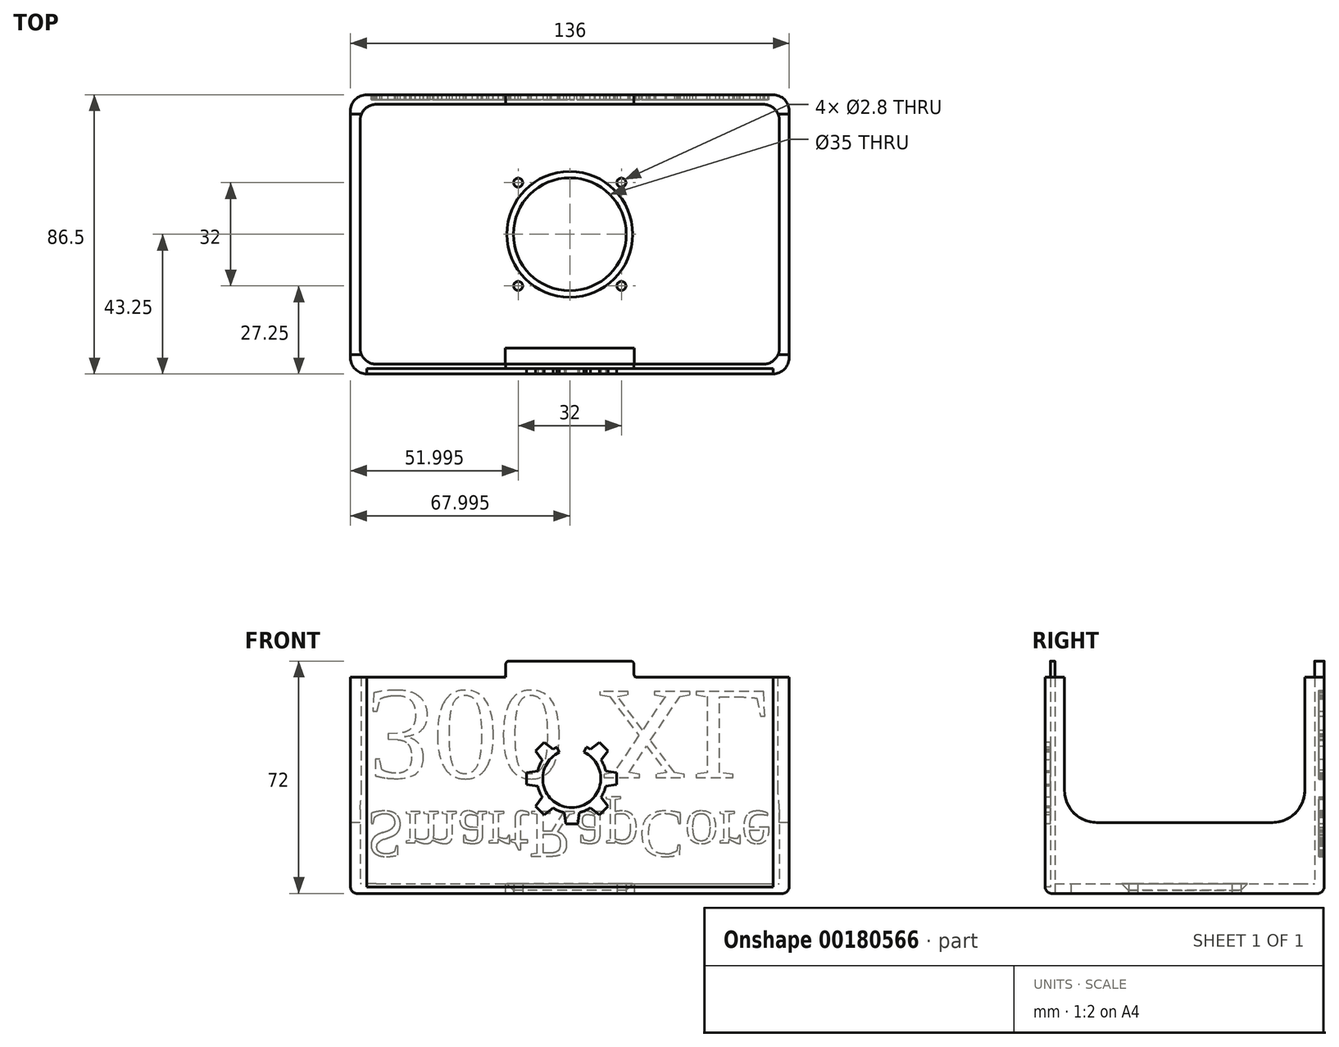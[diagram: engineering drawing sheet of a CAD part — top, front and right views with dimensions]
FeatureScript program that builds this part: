
annotation { "Feature Type Name" : "Feature", "Feature Type Description" : "" }
export const myFeature = defineFeature(function(context is Context, id is Id, definition is map)
    precondition{}
    {
        {
            var Q0;
            Q0=qCreatedBy(makeId("Top.planeOp"),FACE);
            var sketch = newSketch(context, id + "F0", { "sketchPlane" : qUnion([Q0])});
            skLineSegment(sketch, "E0.bottom", {"start": v(-60.37, 0) * mm, "end": v(69.63, 0) * mm});
            skLineSegment(sketch, "E0.top", {"start": v(-60.37, 92.5) * mm, "end": v(69.63, 92.5) * mm});
            skLineSegment(sketch, "E0.left", {"start": v(-60.37, 0) * mm, "end": v(-60.37, 92.5) * mm});
            skLineSegment(sketch, "E0.right", {"start": v(69.63, 0) * mm, "end": v(69.63, 92.5) * mm});
            skLineSegment(sketch, "E1.top", {"start": v(-60.37, 7) * mm, "end": v(69.63, 7) * mm});
            skLineSegment(sketch, "E1.left", {"start": v(-60.37, 0) * mm, "end": v(-60.37, 7) * mm});
            skLineSegment(sketch, "E1.right", {"start": v(69.63, 0) * mm, "end": v(69.63, 7) * mm});
            skLineSegment(sketch, "E2.bottom", {"start": v(-15.37, 7) * mm, "end": v(24.63, 7) * mm});
            skLineSegment(sketch, "E2.top", {"start": v(-15.37, 12) * mm, "end": v(24.63, 12) * mm});
            skLineSegment(sketch, "E2.left", {"start": v(-15.37, 7) * mm, "end": v(-15.37, 12) * mm});
            skLineSegment(sketch, "E2.right", {"start": v(24.63, 7) * mm, "end": v(24.63, 12) * mm});
            skPoint(sketch, "E3", {"position": v(4.63, 92.5) * mm});
            skPoint(sketch, "E4", {"position": v(4.63, 12) * mm});
            skLineSegment(sketch, "E5.top", {"start": v(-60.37, 87.5) * mm, "end": v(69.63, 87.5) * mm});
            skLineSegment(sketch, "E5.left", {"start": v(-60.37, 92.5) * mm, "end": v(-60.37, 87.5) * mm});
            skLineSegment(sketch, "E5.right", {"start": v(69.63, 92.5) * mm, "end": v(69.63, 87.5) * mm});
            skCircle(sketch, "E6", {"center": v(4.63, 47.25) * mm, "radius": 17.5 * mm});
            skCircle(sketch, "E7", {"center": v(20.63, 31.25) * mm, "radius": 1.4 * mm});
            skCircle(sketch, "E8", {"center": v(-11.37, 31.25) * mm, "radius": 1.4 * mm});
            skCircle(sketch, "E9", {"center": v(-11.37, 63.25) * mm, "radius": 1.4 * mm});
            skCircle(sketch, "E10", {"center": v(20.63, 63.25) * mm, "radius": 1.4 * mm});
            skLineSegment(sketch, "E11", {"start": v(20.63, 63.25) * mm, "end": v(20.63, 31.25) * mm, "construction": true});
            skLineSegment(sketch, "E12", {"start": v(-11.37, 63.25) * mm, "end": v(20.63, 63.25) * mm, "construction": true});
            skPoint(sketch, "E13", {"position": v(20.63, 47.25) * mm});
            skPoint(sketch, "E14", {"position": v(4.63, 63.25) * mm});
            skLineSegment(sketch, "E15", {"start": v(20.63, 63.25) * mm, "end": v(20.63, 87.5) * mm, "construction": true});
            skLineSegment(sketch, "E16", {"start": v(20.63, 31.25) * mm, "end": v(20.63, 7) * mm, "construction": true});
            skCircle(sketch, "E17", {"center": v(-30.37, 71.25) * mm, "radius": 3 * mm});
            skCircle(sketch, "E18", {"center": v(-30.37, 23.25) * mm, "radius": 3 * mm});
            skCircle(sketch, "E19", {"center": v(52.63, 71.25) * mm, "radius": 3 * mm});
            skCircle(sketch, "E20", {"center": v(52.63, 23.25) * mm, "radius": 3 * mm});
            skLineSegment(sketch, "E21", {"start": v(-30.37, 71.25) * mm, "end": v(52.63, 71.25) * mm, "construction": true});
            skLineSegment(sketch, "E22", {"start": v(52.63, 71.25) * mm, "end": v(52.63, 23.25) * mm, "construction": true});
            skCircle(sketch, "E23", {"center": v(-30.37, 71.25) * mm, "radius": 1.5 * mm});
            skCircle(sketch, "E24", {"center": v(-30.37, 23.25) * mm, "radius": 1.5 * mm});
            skCircle(sketch, "E25", {"center": v(52.63, 23.25) * mm, "radius": 1.5 * mm});
            skCircle(sketch, "E26", {"center": v(52.63, 71.25) * mm, "radius": 1.5 * mm});
            skLineSegment(sketch, "E27", {"start": v(52.63, 23.25) * mm, "end": v(52.63, 7) * mm, "construction": true});
            skLineSegment(sketch, "E28", {"start": v(52.63, 71.25) * mm, "end": v(52.63, 87.5) * mm, "construction": true});
            skLineSegment(sketch, "E29.bottom", {"start": v(-63.37, 4) * mm, "end": v(72.63, 4) * mm});
            skLineSegment(sketch, "E29.top", {"start": v(-63.37, 90.5) * mm, "end": v(72.63, 90.5) * mm});
            skLineSegment(sketch, "E29.left", {"start": v(-63.37, 4) * mm, "end": v(-63.37, 90.5) * mm});
            skLineSegment(sketch, "E29.right", {"start": v(72.63, 4) * mm, "end": v(72.63, 90.5) * mm});
            skLineSegment(sketch, "E30", {"start": v(4.63, 87.5) * mm, "end": v(4.63, 90.5) * mm});
            skPoint(sketch, "E30.startSnap0", {"position": v(4.63, 90.5) * mm});
            skLineSegment(sketch, "E31", {"start": v(-60.37, 27.6) * mm, "end": v(-63.37, 27.6) * mm});
            skLineSegment(sketch, "E32", {"start": v(14.88, 7) * mm, "end": v(14.88, 4) * mm});
            skLineSegment(sketch, "E33", {"start": v(69.63, 53.4) * mm, "end": v(72.63, 53.4) * mm});
            skLineSegment(sketch, "E34", {"start": v(-30.37, 71.25) * mm, "end": v(-60.37, 71.25) * mm});
            skSolve(sketch);
        }
        {
            var Q0;
            {var subQ2=sQuery(id+"F0.wireOp",EDGE,"E0.left");Q0=makeQuery(id+"F0.imprint","IMPRINT",FACE,{"disambiguationData":[TD([[makeQuery(id+"F0.imprint","IMPRINT",EDGE,{"derivedFrom":subQ2}),-1.0]])]});}
            var Q1;
            Q1=makeQuery(id+"F0.imprint","IMPRINT",FACE,{"disambiguationData":[TD([[makeQuery(id+"F0.imprint","IMPRINT",EDGE,{"derivedFrom":sQuery(id+"F0.wireOp",EDGE,"E2.bottom")}),1.0]])]});
            var Q2;
            Q2=makeQuery(id+"F0.imprint","IMPRINT",FACE,{"disambiguationData":[TD([[makeQuery(id+"F0.imprint","IMPRINT",EDGE,{"derivedFrom":sQuery(id+"F0.wireOp",EDGE,"E17")}),1.0]])]});
            var Q3;
            Q3=makeQuery(id+"F0.imprint","IMPRINT",FACE,{"disambiguationData":[TD([[makeQuery(id+"F0.imprint","IMPRINT",EDGE,{"derivedFrom":sQuery(id+"F0.wireOp",EDGE,"E23")}),1.0]])]});
            var Q4;
            Q4=makeQuery(id+"F0.imprint","IMPRINT",FACE,{"disambiguationData":[TD([[makeQuery(id+"F0.imprint","IMPRINT",EDGE,{"derivedFrom":sQuery(id+"F0.wireOp",EDGE,"E19")}),1.0]])]});
            var Q5;
            Q5=makeQuery(id+"F0.imprint","IMPRINT",FACE,{"disambiguationData":[TD([[makeQuery(id+"F0.imprint","IMPRINT",EDGE,{"derivedFrom":sQuery(id+"F0.wireOp",EDGE,"E26")}),1.0]])]});
            var Q6;
            Q6=makeQuery(id+"F0.imprint","IMPRINT",FACE,{"disambiguationData":[TD([[makeQuery(id+"F0.imprint","IMPRINT",EDGE,{"derivedFrom":sQuery(id+"F0.wireOp",EDGE,"E20")}),1.0]])]});
            var Q7;
            Q7=makeQuery(id+"F0.imprint","IMPRINT",FACE,{"disambiguationData":[TD([[makeQuery(id+"F0.imprint","IMPRINT",EDGE,{"derivedFrom":sQuery(id+"F0.wireOp",EDGE,"E25")}),1.0]])]});
            var Q8;
            Q8=makeQuery(id+"F0.imprint","IMPRINT",FACE,{"disambiguationData":[TD([[makeQuery(id+"F0.imprint","IMPRINT",EDGE,{"derivedFrom":sQuery(id+"F0.wireOp",EDGE,"E18")}),1.0]])]});
            var Q9;
            Q9=makeQuery(id+"F0.imprint","IMPRINT",FACE,{"disambiguationData":[TD([[makeQuery(id+"F0.imprint","IMPRINT",EDGE,{"derivedFrom":sQuery(id+"F0.wireOp",EDGE,"E24")}),1.0]])]});
            extrude(context, id + "F1", {"entities" : qUnion([Q0, Q1, Q2, Q3, Q4, Q5, Q6, Q7, Q8, Q9]), "depth" : 3 * mm});
        }
        {
            var Q0;
            {var subQ3=sQuery(id+"F0.wireOp",EDGE,"E31");Q0=makeQuery(id+"F0.imprint","IMPRINT",FACE,{"disambiguationData":[TD([[makeQuery(id+"F0.imprint","IMPRINT",EDGE,{"derivedFrom":subQ3}),-1.0]])]});}
            var Q1;
            {var subQ3=sQuery(id+"F0.wireOp",EDGE,"E30");Q1=makeQuery(id+"F0.imprint","IMPRINT",FACE,{"disambiguationData":[TD([[makeQuery(id+"F0.imprint","IMPRINT",EDGE,{"derivedFrom":subQ3}),1.0]])]});}
            var Q2;
            {var subQ3=sQuery(id+"F0.wireOp",EDGE,"E30");Q2=makeQuery(id+"F0.imprint","IMPRINT",FACE,{"disambiguationData":[TD([[makeQuery(id+"F0.imprint","IMPRINT",EDGE,{"derivedFrom":subQ3}),-1.0]])]});}
            var Q3;
            {var subQ3=sQuery(id+"F0.wireOp",EDGE,"E33");Q3=makeQuery(id+"F0.imprint","IMPRINT",FACE,{"disambiguationData":[TD([[makeQuery(id+"F0.imprint","IMPRINT",EDGE,{"derivedFrom":subQ3}),1.0]])]});}
            var Q4;
            {var subQ3=sQuery(id+"F0.wireOp",EDGE,"E33");Q4=makeQuery(id+"F0.imprint","IMPRINT",FACE,{"disambiguationData":[TD([[makeQuery(id+"F0.imprint","IMPRINT",EDGE,{"derivedFrom":subQ3}),-1.0]])]});}
            var Q5;
            {var subQ0=sQuery(id+"F0.wireOp",EDGE,"E32");Q5=makeQuery(id+"F0.imprint","IMPRINT",FACE,{"disambiguationData":[TD([[makeQuery(id+"F0.imprint","IMPRINT",EDGE,{"derivedFrom":subQ0}),1.0]])]});}
            var Q6;
            {var subQ3=sQuery(id+"F0.wireOp",EDGE,"E32");Q6=makeQuery(id+"F0.imprint","IMPRINT",FACE,{"disambiguationData":[TD([[makeQuery(id+"F0.imprint","IMPRINT",EDGE,{"derivedFrom":subQ3}),-1.0]])]});}
            var Q7;
            {var subQ3=sQuery(id+"F0.wireOp",EDGE,"E31");Q7=makeQuery(id+"F0.imprint","IMPRINT",FACE,{"disambiguationData":[TD([[makeQuery(id+"F0.imprint","IMPRINT",EDGE,{"derivedFrom":subQ3}),1.0]])]});}
            extrude(context, id + "F2", {"entities" : qUnion([Q0, Q1, Q2, Q3, Q4, Q5, Q6, Q7]), "operationType" : NewBodyOperationType.ADD, "depth" : 67 * mm});
        }
        {
            var Q0;
            Q0=makeQuery(id+"F2.opExtrude","SWEPT_FACE",FACE,{"disambiguationData":[OSD([sQuery(id+"F0.wireOp",EDGE,"E29.left")])]});
            var sketch = newSketch(context, id + "F3", { "sketchPlane" : qUnion([Q0])});
            skCircle(sketch, "E35", {"center": v(-20, 31.97) * mm, "radius": 10 * mm});
            skPoint(sketch, "E36", {"position": v(-57.96, 0) * mm});
            skLineSegment(sketch, "E37", {"start": v(-30, 31.97) * mm, "end": v(-30, 67) * mm});
            skLineSegment(sketch, "E38", {"start": v(-10, 31.97) * mm, "end": v(-10, 67) * mm});
            skCircle(sketch, "E39", {"center": v(-74.5, 31.97) * mm, "radius": 10 * mm});
            skLineSegment(sketch, "E40", {"start": v(-84.5, 31.97) * mm, "end": v(-84.5, 67) * mm});
            skLineSegment(sketch, "E41", {"start": v(-64.5, 31.97) * mm, "end": v(-64.5, 46.86) * mm});
            skLineSegment(sketch, "E42", {"start": v(-20, 21.97) * mm, "end": v(-74.5, 21.97) * mm});
            skLineSegment(sketch, "E43", {"start": v(-64.5, 31.97) * mm, "end": v(-30, 31.97) * mm});
            skPoint(sketch, "E44", {"position": v(-47.25, 31.97) * mm});
            skPoint(sketch, "E45", {"position": v(-47.25, 67) * mm});
            skSolve(sketch);
        }
        {
            var Q0;
            Q0=makeQuery(id+"F3.imprint","IMPRINT",FACE,{"disambiguationData":[TD([[makeQuery(id+"F3.imprint","IMPRINT",EDGE,{"derivedFrom":sQuery(id+"F3.wireOp",EDGE,"Rx419f1T-JsYL-VPEE-dF0Y-VFoqTHM8m6fg.bottom")}),1.0]])]});
            var Q1;
            Q1=makeQuery(id+"F3.imprint","IMPRINT",FACE,{"disambiguationData":[TD([[makeQuery(id+"F3.imprint","IMPRINT",EDGE,{"derivedFrom":sQuery(id+"F3.wireOp",EDGE,"E35")}),1.0]])]});
            var Q2;
            {var subQ0=sQuery(id+"F3.wireOp",EDGE,"E37");Q2=makeQuery(id+"F3.imprint","IMPRINT",FACE,{"disambiguationData":[TD([[makeQuery(id+"F3.imprint","IMPRINT",EDGE,{"derivedFrom":subQ0}),-1.0]])]});}
            var Q3;
            {var subQ0=sQuery(id+"F3.wireOp",EDGE,"E39");var subQ1=makeQuery(id+"F3.imprint","INTERSECT",VERTEX,{"derivedFrom":[subQ0,sQuery(id+"F3.wireOp",EDGE,"E40")]});Q3=makeQuery(id+"F3.imprint","IMPRINT",FACE,{"disambiguationData":[TD([[makeQuery(id+"F3.imprint","IMPRINT",EDGE,{"disambiguationData":[TD([[subQ1,-1.0]])],"derivedFrom":subQ0}),1.0]])]});}
            var Q4;
            {var subQ0=sQuery(id+"F3.wireOp",EDGE,"E40");Q4=makeQuery(id+"F3.imprint","IMPRINT",FACE,{"disambiguationData":[TD([[makeQuery(id+"F3.imprint","IMPRINT",EDGE,{"derivedFrom":subQ0}),-1.0]])]});}
            var Q5;
            {var subQ0=sQuery(id+"F3.wireOp",EDGE,"E37");Q5=makeQuery(id+"F3.imprint","IMPRINT",FACE,{"disambiguationData":[TD([[makeQuery(id+"F3.imprint","IMPRINT",EDGE,{"derivedFrom":subQ0}),1.0]])]});}
            var Q6;
            {var subQ2=sQuery(id+"F3.wireOp",EDGE,"E42");Q6=makeQuery(id+"F3.imprint","IMPRINT",FACE,{"disambiguationData":[TD([[makeQuery(id+"F3.imprint","IMPRINT",EDGE,{"derivedFrom":subQ2}),-1.0]])]});}
            extrude(context, id + "F4", {"entities" : qUnion([Q0, Q1, Q2, Q3, Q4, Q5, Q6]), "operationType" : NewBodyOperationType.REMOVE, "endBound" : BoundingType.THROUGH_ALL, "oppositeDirection" : true, "depth" : 25 * mm});
        }
        {
            var Q0;
            Q0=makeQuery(id+"F2.opExtrude","CAP_FACE",FACE,{"disambiguationData":[OSD([sQuery(id+"F0.wireOp",EDGE,"E0.left"),sQuery(id+"F0.wireOp",EDGE,"E0.right"),sQuery(id+"F0.wireOp",EDGE,"E1.top"),sQuery(id+"F0.wireOp",EDGE,"E2.bottom"),sQuery(id+"F0.wireOp",EDGE,"E5.top"),sQuery(id+"F0.wireOp",EDGE,"E29.bottom"),sQuery(id+"F0.wireOp",EDGE,"E29.top"),sQuery(id+"F0.wireOp",EDGE,"E29.left"),sQuery(id+"F0.wireOp",EDGE,"E29.right")])],"isStart":false});
            var sketch = newSketch(context, id + "F5", { "sketchPlane" : qUnion([Q0])});
            skLineSegment(sketch, "E46.bottom", {"start": v(-15.22, 7) * mm, "end": v(24.48, 7) * mm});
            skLineSegment(sketch, "E46.top", {"start": v(-15.22, 4) * mm, "end": v(24.48, 4) * mm});
            skLineSegment(sketch, "E46.left", {"start": v(-15.22, 7) * mm, "end": v(-15.22, 4) * mm});
            skLineSegment(sketch, "E46.right", {"start": v(24.48, 7) * mm, "end": v(24.48, 4) * mm});
            skPoint(sketch, "E47", {"position": v(4.63, 87.5) * mm});
            skPoint(sketch, "E48", {"position": v(4.63, 7) * mm});
            skSolve(sketch);
        }
        {
            var Q0;
            {var subQ0=sQuery(id+"F0.wireOp",EDGE,"E29.top");var subQ1=sQuery(id+"F0.wireOp",EDGE,"E5.top");var subQ2=sQuery(id+"F0.wireOp",EDGE,"E0.right");var subQ3=sQuery(id+"F0.wireOp",EDGE,"E0.left");var subQ4=sQuery(id+"F0.wireOp",EDGE,"E29.left");var subQ5=sQuery(id+"F0.wireOp",EDGE,"E29.right");Q0=makeQuery(id+"F4.boolean.opBoolean","SPLIT",FACE,{"disambiguationData":[TD([makeQuery(id+"F2.opExtrude","SWEPT_FACE",FACE,{"disambiguationData":[OSD([subQ1])]})])],"derivedFrom":makeQuery(id+"F2.opExtrude","CAP_FACE",FACE,{"disambiguationData":[OSD([subQ3,subQ2,sQuery(id+"F0.wireOp",EDGE,"E1.top"),sQuery(id+"F0.wireOp",EDGE,"E2.bottom"),subQ1,sQuery(id+"F0.wireOp",EDGE,"E29.bottom"),subQ0,subQ4,subQ5])],"isStart":false})});}
            var sketch = newSketch(context, id + "F6", { "sketchPlane" : qUnion([Q0])});
            skPoint(sketch, "E49", {"position": v(4.63, 87.5) * mm});
            skLineSegment(sketch, "E50.bottom", {"start": v(24.48, 87.5) * mm, "end": v(-15.22, 87.5) * mm});
            skLineSegment(sketch, "E50.top", {"start": v(24.48, 90.5) * mm, "end": v(-15.22, 90.5) * mm});
            skLineSegment(sketch, "E50.left", {"start": v(24.48, 87.5) * mm, "end": v(24.48, 90.5) * mm});
            skLineSegment(sketch, "E50.right", {"start": v(-15.22, 87.5) * mm, "end": v(-15.22, 90.5) * mm});
            skPoint(sketch, "E51", {"position": v(4.63, 90.5) * mm});
            skSolve(sketch);
        }
        {
            var Q0;
            Q0=qSketchRegion(id+"F5",true);
            var Q1;
            Q1=makeQuery(id+"F6.imprint","IMPRINT",FACE,{"disambiguationData":[TD([[makeQuery(id+"F6.imprint","IMPRINT",EDGE,{"derivedFrom":sQuery(id+"F6.wireOp",EDGE,"E50.bottom")}),1.0]])]});
            extrude(context, id + "F7", {"entities" : qUnion([Q0, Q1]), "operationType" : NewBodyOperationType.ADD, "depth" : 5 * mm});
        }
        {
            var Q0;
            Q0=makeQuery(id+"F7.opExtrude","CAP_EDGE",EDGE,{"disambiguationData":[OSD([sQuery(id+"F5.wireOp",EDGE,"E46.left")])],"isStart":true});
            var Q1;
            Q1=makeQuery(id+"F7.opExtrude","CAP_EDGE",EDGE,{"disambiguationData":[OSD([sQuery(id+"F5.wireOp",EDGE,"E46.left")])],"isStart":false});
            var Q2;
            Q2=makeQuery(id+"F7.opExtrude","CAP_EDGE",EDGE,{"disambiguationData":[OSD([sQuery(id+"F5.wireOp",EDGE,"E46.right")])],"isStart":false});
            var Q3;
            Q3=makeQuery(id+"F7.opExtrude","CAP_EDGE",EDGE,{"disambiguationData":[OSD([sQuery(id+"F5.wireOp",EDGE,"E46.right")])],"isStart":true});
            var Q4;
            Q4=makeQuery(id+"F7.opExtrude","CAP_EDGE",EDGE,{"disambiguationData":[OSD([sQuery(id+"F6.wireOp",EDGE,"E50.right")])],"isStart":true});
            var Q5;
            Q5=makeQuery(id+"F7.opExtrude","CAP_EDGE",EDGE,{"disambiguationData":[OSD([sQuery(id+"F6.wireOp",EDGE,"E50.right")])],"isStart":false});
            var Q6;
            Q6=makeQuery(id+"F7.opExtrude","CAP_EDGE",EDGE,{"disambiguationData":[OSD([sQuery(id+"F6.wireOp",EDGE,"E50.left")])],"isStart":false});
            var Q7;
            Q7=makeQuery(id+"F7.opExtrude","CAP_EDGE",EDGE,{"disambiguationData":[OSD([sQuery(id+"F6.wireOp",EDGE,"E50.left")])],"isStart":true});
            fillet(context, id + "F8", {"entities" : qUnion([Q0, Q1, Q2, Q3, Q4, Q5, Q6, Q7]), "radius" : 1 * mm, "tangentPropagation" : true, "allowEdgeOverflow" : false});
        }
        {
            var Q0;
            Q0=makeQuery(id+"F2.opExtrude","SWEPT_EDGE",EDGE,{"disambiguationData":[OSD([sQuery(id+"F0.wireOp",EDGE,"E29.bottom"),sQuery(id+"F0.wireOp",EDGE,"E29.right")])]});
            var Q1;
            Q1=makeQuery(id+"F2.opExtrude","SWEPT_EDGE",EDGE,{"disambiguationData":[OSD([sQuery(id+"F0.wireOp",EDGE,"E29.top"),sQuery(id+"F0.wireOp",EDGE,"E29.right")])]});
            var Q2;
            Q2=makeQuery(id+"F2.opExtrude","SWEPT_EDGE",EDGE,{"disambiguationData":[OSD([sQuery(id+"F0.wireOp",EDGE,"E29.top"),sQuery(id+"F0.wireOp",EDGE,"E29.left")])]});
            var Q3;
            Q3=makeQuery(id+"F2.opExtrude","SWEPT_EDGE",EDGE,{"disambiguationData":[OSD([sQuery(id+"F0.wireOp",EDGE,"E29.bottom"),sQuery(id+"F0.wireOp",EDGE,"E29.left")])]});
            var Q4;
            Q4=makeQuery(id+"F2.opExtrude","SWEPT_EDGE",EDGE,{"disambiguationData":[OSD([sQuery(id+"F0.wireOp",EDGE,"E0.left"),sQuery(id+"F0.wireOp",EDGE,"E1.top"),sQuery(id+"F0.wireOp",EDGE,"E1.left")])]});
            var Q5;
            Q5=makeQuery(id+"F2.opExtrude","SWEPT_EDGE",EDGE,{"disambiguationData":[OSD([sQuery(id+"F0.wireOp",EDGE,"E0.left"),sQuery(id+"F0.wireOp",EDGE,"E5.top"),sQuery(id+"F0.wireOp",EDGE,"E5.left")])]});
            var Q6;
            Q6=makeQuery(id+"F2.opExtrude","SWEPT_EDGE",EDGE,{"disambiguationData":[OSD([sQuery(id+"F0.wireOp",EDGE,"E0.right"),sQuery(id+"F0.wireOp",EDGE,"E5.top"),sQuery(id+"F0.wireOp",EDGE,"E5.right")])]});
            var Q7;
            Q7=makeQuery(id+"F2.opExtrude","SWEPT_EDGE",EDGE,{"disambiguationData":[OSD([sQuery(id+"F0.wireOp",EDGE,"E0.right"),sQuery(id+"F0.wireOp",EDGE,"E1.top"),sQuery(id+"F0.wireOp",EDGE,"E1.right")])]});
            fillet(context, id + "F9", {"entities" : qUnion([Q0, Q1, Q2, Q3, Q4, Q5, Q6, Q7]), "radius" : 5 * mm, "tangentPropagation" : true, "allowEdgeOverflow" : false});
        }
        {
            var Q0;
            Q0=makeQuery(id+"F1.opExtrude","CAP_EDGE",EDGE,{"disambiguationData":[OSD([sQuery(id+"F0.wireOp",EDGE,"E5.top")])],"isStart":false});
            var Q1;
            Q1=makeQuery(id+"F2.opExtrude","CAP_EDGE",EDGE,{"disambiguationData":[OSD([sQuery(id+"F0.wireOp",EDGE,"E29.bottom")])],"isStart":true});
            fillet(context, id + "F10", {"entities" : qUnion([Q0, Q1]), "radius" : 2 * mm, "tangentPropagation" : true, "allowEdgeOverflow" : false});
        }
        {
            var Q0;
            Q0=makeQuery(id+"F7.boolean.opBoolean","MERGE",FACE,{"derivedFrom":[makeQuery(id+"F2.opExtrude","SWEPT_FACE",FACE,{"disambiguationData":[OSD([sQuery(id+"F0.wireOp",EDGE,"E29.bottom")])]}),makeQuery(id+"F7.opExtrude","SWEPT_FACE",FACE,{"disambiguationData":[OSD([sQuery(id+"F5.wireOp",EDGE,"E46.top")])]})]});
            var sketch = newSketch(context, id + "F11", { "sketchPlane" : qUnion([Q0])});
            skLineSegment(sketch, "E52", {"start": v(4.57, 42.98) * mm, "end": v(4.57, 28.17) * mm});
            skLineSegment(sketch, "E53", {"start": v(8.1, 36.85) * mm, "end": v(8.1, 42.41) * mm});
            skLineSegment(sketch, "E54", {"start": v(10.33, 36.85) * mm, "end": v(8.1, 36.85) * mm});
            skLineSegment(sketch, "E55", {"start": v(1.05, 34.29) * mm, "end": v(2.33, 34.29) * mm});
            skArc(sketch, "E56", {"start": v(0.4, 34.5) * mm, "mid": v(1.1, 32.87) * mm, "end": v(2.31, 31.6) * mm});
            skLineSegment(sketch, "E57", {"start": v(10.33, 34.29) * mm, "end": v(8.1, 34.29) * mm});
            skLineSegment(sketch, "E58", {"start": v(2.33, 34.29) * mm, "end": v(2.33, 31.62) * mm});
            skLineSegment(sketch, "E59", {"start": v(1.05, 36.86) * mm, "end": v(1.05, 34.29) * mm});
            skLineSegment(sketch, "E60", {"start": v(2.33, 36.86) * mm, "end": v(1.05, 36.86) * mm});
            skArc(sketch, "E61", {"start": v(5.85, 42.98) * mm, "mid": v(7, 42.79) * mm, "end": v(8.1, 42.42) * mm});
            skLineSegment(sketch, "E62", {"start": v(8.1, 42.42) * mm, "end": v(8.1, 42.41) * mm});
            skArc(sketch, "E63", {"start": v(10.33, 30.28) * mm, "mid": v(12.58, 35.57) * mm, "end": v(10.33, 40.87) * mm});
            skLineSegment(sketch, "E64", {"start": v(10.33, 36.85) * mm, "end": v(10.33, 40.87) * mm});
            skArc(sketch, "E65", {"start": v(10.97, 26.46) * mm, "mid": v(9.34, 25.61) * mm, "end": v(7.59, 25.06) * mm});
            skLineSegment(sketch, "E66", {"start": v(7.08, 21.57) * mm, "end": v(7.59, 25.06) * mm});
            skLineSegment(sketch, "E67", {"start": v(13.82, 24.38) * mm, "end": v(13.8, 24.35) * mm});
            skLineSegment(sketch, "E68", {"start": v(10.97, 26.46) * mm, "end": v(13.8, 24.35) * mm});
            skLineSegment(sketch, "E69", {"start": v(14.33, 29.81) * mm, "end": v(16.43, 27) * mm});
            skLineSegment(sketch, "E70", {"start": v(13.8, 24.35) * mm, "end": v(16.43, 27) * mm});
            skArc(sketch, "E71", {"start": v(14.33, 29.81) * mm, "mid": v(15.17, 31.45) * mm, "end": v(15.73, 33.2) * mm});
            skLineSegment(sketch, "E72", {"start": v(19.21, 33.7) * mm, "end": v(15.73, 33.2) * mm});
            skArc(sketch, "E73", {"start": v(4.57, 42.98) * mm, "mid": v(3.43, 42.79) * mm, "end": v(2.33, 42.42) * mm});
            skLineSegment(sketch, "E74", {"start": v(2.33, 36.86) * mm, "end": v(2.33, 42.42) * mm});
            skArc(sketch, "E75", {"start": v(4.57, 28.17) * mm, "mid": v(0.32, 29.98) * mm, "end": v(-2.04, 33.96) * mm});
            skArc(sketch, "E76", {"start": v(5.85, 28.17) * mm, "mid": v(7, 28.36) * mm, "end": v(8.1, 28.72) * mm});
            skArc(sketch, "E77", {"start": v(1.41, 43.72) * mm, "mid": v(5.21, 26.58) * mm, "end": v(9.02, 43.72) * mm});
            skArc(sketch, "E78", {"start": v(10.97, 44.68) * mm, "mid": v(10.38, 45.03) * mm, "end": v(9.77, 45.34) * mm});
            skLineSegment(sketch, "E79", {"start": v(9.77, 45.34) * mm, "end": v(9.02, 43.72) * mm});
            skLineSegment(sketch, "E80", {"start": v(19.21, 33.7) * mm, "end": v(19.21, 37.44) * mm});
            skLineSegment(sketch, "E81", {"start": v(19.21, 37.44) * mm, "end": v(15.73, 37.94) * mm});
            skLineSegment(sketch, "E82", {"start": v(13.8, 46.8) * mm, "end": v(10.97, 44.68) * mm});
            skLineSegment(sketch, "E83", {"start": v(13.8, 46.8) * mm, "end": v(16.43, 44.15) * mm});
            skLineSegment(sketch, "E84", {"start": v(14.33, 41.32) * mm, "end": v(16.43, 44.15) * mm});
            skArc(sketch, "E85", {"start": v(14.33, 41.32) * mm, "mid": v(15.17, 39.69) * mm, "end": v(15.73, 37.94) * mm});
            skLineSegment(sketch, "E86", {"start": v(15.73, 37.94) * mm, "end": v(15.73, 37.94) * mm});
            skLineSegment(sketch, "E87", {"start": v(1.41, 43.72) * mm, "end": v(0.65, 45.33) * mm});
            skLineSegment(sketch, "E88", {"start": v(7.08, 21.57) * mm, "end": v(3.35, 21.57) * mm});
            skLineSegment(sketch, "E89", {"start": v(3.35, 21.57) * mm, "end": v(2.84, 25.06) * mm});
            skArc(sketch, "E90", {"start": v(2.84, 25.06) * mm, "mid": v(1.1, 25.61) * mm, "end": v(-0.54, 26.46) * mm});
            skLineSegment(sketch, "E91", {"start": v(-0.54, 26.46) * mm, "end": v(-3.37, 24.35) * mm});
            skArc(sketch, "E92", {"start": v(0.65, 45.33) * mm, "mid": v(0.04, 45.03) * mm, "end": v(-0.54, 44.69) * mm});
            skLineSegment(sketch, "E93", {"start": v(-0.54, 44.69) * mm, "end": v(-3.37, 46.8) * mm});
            skArc(sketch, "E94", {"start": v(-3.9, 41.32) * mm, "mid": v(-4.74, 39.7) * mm, "end": v(-5.3, 37.94) * mm});
            skLineSegment(sketch, "E95", {"start": v(-3.9, 41.32) * mm, "end": v(-6, 44.15) * mm});
            skLineSegment(sketch, "E96", {"start": v(-3.37, 46.8) * mm, "end": v(-6, 44.15) * mm});
            skLineSegment(sketch, "E97", {"start": v(-8.78, 33.7) * mm, "end": v(-8.78, 37.44) * mm});
            skLineSegment(sketch, "E98", {"start": v(-5.3, 37.94) * mm, "end": v(-8.78, 37.44) * mm});
            skLineSegment(sketch, "E99", {"start": v(-3.9, 29.82) * mm, "end": v(-6, 27) * mm});
            skLineSegment(sketch, "E100", {"start": v(-3.37, 24.35) * mm, "end": v(-6, 27) * mm});
            skArc(sketch, "E101", {"start": v(-3.9, 29.82) * mm, "mid": v(-4.74, 31.45) * mm, "end": v(-5.3, 33.2) * mm});
            skLineSegment(sketch, "E102", {"start": v(-5.3, 33.2) * mm, "end": v(-8.78, 33.7) * mm});
            skLineSegment(sketch, "E103", {"start": v(2.33, 31.62) * mm, "end": v(2.33, 31.58) * mm});
            skLineSegment(sketch, "E104", {"start": v(2.33, 31.58) * mm, "end": v(2.31, 31.6) * mm});
            skLineSegment(sketch, "E105", {"start": v(0.4, 34.5) * mm, "end": v(-2.04, 33.96) * mm});
            skLineSegment(sketch, "E106", {"start": v(5.85, 42.98) * mm, "end": v(5.85, 28.17) * mm});
            skLineSegment(sketch, "E107", {"start": v(8.1, 34.29) * mm, "end": v(8.1, 28.72) * mm});
            skLineSegment(sketch, "E108", {"start": v(10.33, 30.28) * mm, "end": v(10.33, 34.29) * mm});
            skSolve(sketch);
        }
        {
            var Q0;
            Q0=makeQuery(id+"F11.imprint","IMPRINT",FACE,{"disambiguationData":[TD([[makeQuery(id+"F11.imprint","IMPRINT",EDGE,{"derivedFrom":sQuery(id+"F11.wireOp",EDGE,"E52")}),-1.0]])]});
            var Q1;
            Q1=makeQuery(id+"F11.imprint","IMPRINT",FACE,{"disambiguationData":[TD([[makeQuery(id+"F11.imprint","IMPRINT",EDGE,{"derivedFrom":sQuery(id+"F11.wireOp",EDGE,"E53")}),1.0]])]});
            var Q2;
            Q2=makeQuery(id+"F11.imprint","IMPRINT",FACE,{"disambiguationData":[TD([[makeQuery(id+"F11.imprint","IMPRINT",EDGE,{"derivedFrom":sQuery(id+"F11.wireOp",EDGE,"E52")}),-1.0]])]});
            var Q3;
            Q3=makeQuery(id+"F11.imprint","IMPRINT",FACE,{"disambiguationData":[TD([[makeQuery(id+"F11.imprint","IMPRINT",EDGE,{"derivedFrom":sQuery(id+"F11.wireOp",EDGE,"E53")}),1.0]])]});
            var Q4;
            Q4=makeQuery(id+"F11.imprint","IMPRINT",FACE,{"disambiguationData":[TD([[makeQuery(id+"F11.imprint","IMPRINT",EDGE,{"derivedFrom":sQuery(id+"F11.wireOp",EDGE,"E65")}),-1.0]])]});
            extrude(context, id + "F12", {"entities" : qUnion([Q0, Q1, Q2, Q3, Q4]), "operationType" : NewBodyOperationType.REMOVE, "oppositeDirection" : true, "depth" : 1.6 * mm});
        }
        {
            var Q0;
            Q0=makeQuery(id+"F1.opExtrude","CAP_EDGE",EDGE,{"disambiguationData":[OSD([sQuery(id+"F0.wireOp",EDGE,"E6")])],"isStart":false});
            chamfer(context, id + "F13", {"entities" : qUnion([Q0]), "width" : 2 * mm, "tangentPropagation" : true});
        }
        {
            var Q0;
            Q0=makeQuery(id+"F7.boolean.opBoolean","MERGE",FACE,{"derivedFrom":[makeQuery(id+"F2.opExtrude","SWEPT_FACE",FACE,{"disambiguationData":[OSD([sQuery(id+"F0.wireOp",EDGE,"E29.top")])]}),makeQuery(id+"F7.opExtrude","SWEPT_FACE",FACE,{"disambiguationData":[OSD([sQuery(id+"F6.wireOp",EDGE,"E50.top")])]})]});
            var sketch = newSketch(context, id + "F14", { "sketchPlane" : qUnion([Q0])});
            skText(sketch, "E109", { "text": "300 XL", "fontName": "Tinos-Regular.ttf"});
            skText(sketch, "E110", { "text": "SmartRapCore", "fontName": "Tinos-Regular.ttf"});
            const initialGuessF14  = {"E109": [0.05837, 0.0626, -1, 0, 0.0294], "E110": [0.05837, 0.02537, -1, 0, 0.0152]};
            skSetInitialGuess(sketch, initialGuessF14);
            skSolve(sketch);
        }
        {
            var Q0;
            Q0=makeQuery(id+"F14.imprint","IMPRINT",FACE,{"disambiguationData":[TD([[makeQuery(id+"F14.imprint","IMPRINT",EDGE,{"derivedFrom":sQuery(id+"F14.wireOp",EDGE,"E109.sketch_text.stroke-31")}),-1.0]])]});
            var Q1;
            Q1=makeQuery(id+"F14.imprint","IMPRINT",FACE,{"disambiguationData":[TD([[makeQuery(id+"F14.imprint","IMPRINT",EDGE,{"derivedFrom":sQuery(id+"F14.wireOp",EDGE,"E109.sketch_text.stroke-46")}),-1.0]])]});
            var Q2;
            Q2=makeQuery(id+"F14.imprint","IMPRINT",FACE,{"disambiguationData":[TD([[makeQuery(id+"F14.imprint","IMPRINT",EDGE,{"derivedFrom":sQuery(id+"F14.wireOp",EDGE,"E109.sketch_text.stroke-61")}),-1.0]])]});
            var Q3;
            Q3=makeQuery(id+"F14.imprint","IMPRINT",FACE,{"disambiguationData":[TD([[makeQuery(id+"F14.imprint","IMPRINT",EDGE,{"derivedFrom":sQuery(id+"F14.wireOp",EDGE,"E109.sketch_text.stroke-89")}),-1.0]])]});
            var Q4;
            Q4=makeQuery(id+"F14.imprint","IMPRINT",FACE,{"disambiguationData":[TD([[makeQuery(id+"F14.imprint","IMPRINT",EDGE,{"derivedFrom":sQuery(id+"F14.wireOp",EDGE,"E109.sketch_text.stroke-0")}),-1.0]])]});
            var Q5;
            Q5=makeQuery(id+"F14.imprint","IMPRINT",FACE,{"disambiguationData":[TD([[makeQuery(id+"F14.imprint","IMPRINT",EDGE,{"derivedFrom":sQuery(id+"F14.wireOp",EDGE,"E110.sketch_text.stroke-0")}),-1.0]])]});
            var Q6;
            Q6=makeQuery(id+"F14.imprint","IMPRINT",FACE,{"disambiguationData":[TD([[makeQuery(id+"F14.imprint","IMPRINT",EDGE,{"derivedFrom":sQuery(id+"F14.wireOp",EDGE,"E110.sketch_text.stroke-36")}),-1.0]])]});
            var Q7;
            Q7=makeQuery(id+"F14.imprint","IMPRINT",FACE,{"disambiguationData":[TD([[makeQuery(id+"F14.imprint","IMPRINT",EDGE,{"derivedFrom":sQuery(id+"F14.wireOp",EDGE,"E110.sketch_text.stroke-77")}),-1.0]])]});
            var Q8;
            Q8=makeQuery(id+"F14.imprint","IMPRINT",FACE,{"disambiguationData":[TD([[makeQuery(id+"F14.imprint","IMPRINT",EDGE,{"derivedFrom":sQuery(id+"F14.wireOp",EDGE,"E110.sketch_text.stroke-105")}),-1.0]])]});
            var Q9;
            Q9=makeQuery(id+"F14.imprint","IMPRINT",FACE,{"disambiguationData":[TD([[makeQuery(id+"F14.imprint","IMPRINT",EDGE,{"derivedFrom":sQuery(id+"F14.wireOp",EDGE,"E110.sketch_text.stroke-124")}),-1.0]])]});
            var Q10;
            Q10=makeQuery(id+"F14.imprint","IMPRINT",FACE,{"disambiguationData":[TD([[makeQuery(id+"F14.imprint","IMPRINT",EDGE,{"derivedFrom":sQuery(id+"F14.wireOp",EDGE,"E110.sketch_text.stroke-143")}),-1.0]])]});
            var Q11;
            Q11=makeQuery(id+"F14.imprint","IMPRINT",FACE,{"disambiguationData":[TD([[makeQuery(id+"F14.imprint","IMPRINT",EDGE,{"derivedFrom":sQuery(id+"F14.wireOp",EDGE,"E110.sketch_text.stroke-170")}),-1.0]])]});
            var Q12;
            Q12=makeQuery(id+"F14.imprint","IMPRINT",FACE,{"disambiguationData":[TD([[makeQuery(id+"F14.imprint","IMPRINT",EDGE,{"derivedFrom":sQuery(id+"F14.wireOp",EDGE,"E110.sketch_text.stroke-198")}),-1.0]])]});
            var Q13;
            Q13=makeQuery(id+"F14.imprint","IMPRINT",FACE,{"disambiguationData":[TD([[makeQuery(id+"F14.imprint","IMPRINT",EDGE,{"derivedFrom":sQuery(id+"F14.wireOp",EDGE,"E110.sketch_text.stroke-277")}),-1.0]])]});
            var Q14;
            Q14=makeQuery(id+"F14.imprint","IMPRINT",FACE,{"disambiguationData":[TD([[makeQuery(id+"F14.imprint","IMPRINT",EDGE,{"derivedFrom":sQuery(id+"F14.wireOp",EDGE,"E110.sketch_text.stroke-258")}),-1.0]])]});
            var Q15;
            Q15=makeQuery(id+"F14.imprint","IMPRINT",FACE,{"disambiguationData":[TD([[makeQuery(id+"F14.imprint","IMPRINT",EDGE,{"derivedFrom":sQuery(id+"F14.wireOp",EDGE,"E110.sketch_text.stroke-243")}),-1.0]])]});
            var Q16;
            Q16=makeQuery(id+"F14.imprint","IMPRINT",FACE,{"disambiguationData":[TD([[makeQuery(id+"F14.imprint","IMPRINT",EDGE,{"derivedFrom":sQuery(id+"F14.wireOp",EDGE,"E110.sketch_text.stroke-223")}),-1.0]])]});
            extrude(context, id + "F15", {"entities" : qUnion([Q0, Q1, Q2, Q3, Q4, Q5, Q6, Q7, Q8, Q9, Q10, Q11, Q12, Q13, Q14, Q15, Q16]), "operationType" : NewBodyOperationType.REMOVE, "oppositeDirection" : true, "depth" : 1.6 * mm});
        }
    });
